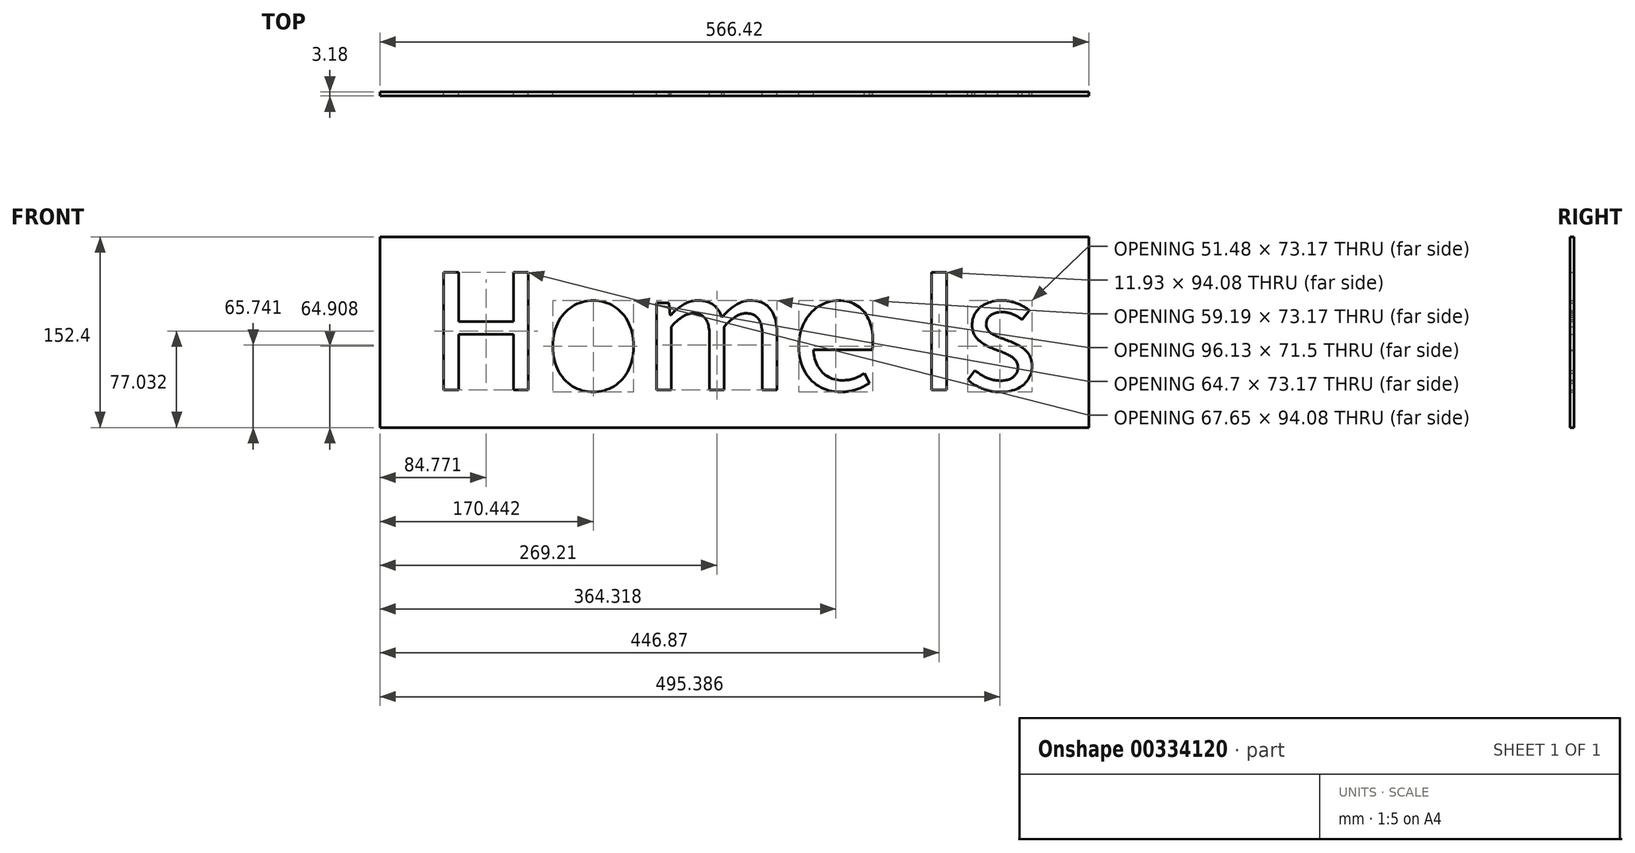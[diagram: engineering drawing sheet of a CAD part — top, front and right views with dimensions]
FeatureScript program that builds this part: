
annotation { "Feature Type Name" : "Feature", "Feature Type Description" : "" }
export const myFeature = defineFeature(function(context is Context, id is Id, definition is map)
    precondition{}
    {
        {
            var Q0;
            Q0=qCreatedBy(makeId("Front.planeOp"),FACE);
            var sketch = newSketch(context, id + "F0", { "sketchPlane" : qUnion([Q0])});
            skLineSegment(sketch, "E0.bottom", {"start": v(-283.2, 76.2) * mm, "end": v(283.21, 76.2) * mm});
            skLineSegment(sketch, "E0.top", {"start": v(-283.21, -76.2) * mm, "end": v(283.21, -76.2) * mm});
            skLineSegment(sketch, "E0.left", {"start": v(-283.21, 76.2) * mm, "end": v(-283.21, -76.2) * mm});
            skLineSegment(sketch, "E0.right", {"start": v(283.21, 76.2) * mm, "end": v(283.21, -76.2) * mm});
            skPoint(sketch, "E0.middle", {"position": v(0, 0) * mm});
            skText(sketch, "E1", { "text": "Home Is", "fontName": "NotoSansCJKtc-Regular.otf"});
            const initialGuessF0  = {"E1": [-0.2451, -0.04621, 1, 0, 0.09242]};
            skSetInitialGuess(sketch, initialGuessF0);
            skSolve(sketch);
        }
        {
            var Q0;
            Q0=qSketchRegion(id+"F0",true);
            extrude(context, id + "F1", {"entities" : qUnion([Q0]), "depth" : 3.17 * mm});
        }
    });
